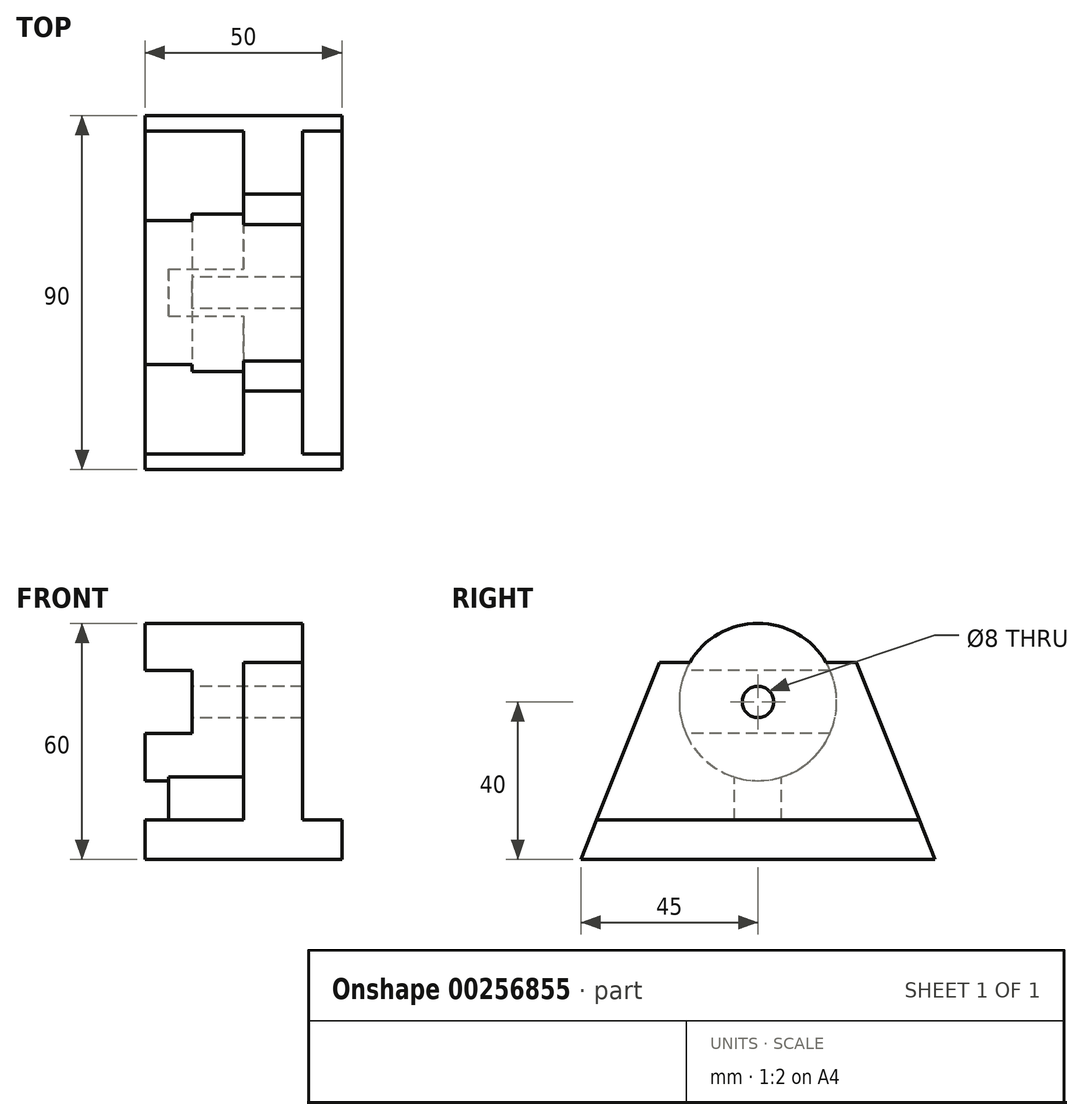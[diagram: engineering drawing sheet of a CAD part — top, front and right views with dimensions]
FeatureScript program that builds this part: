
annotation { "Feature Type Name" : "Feature", "Feature Type Description" : "" }
export const myFeature = defineFeature(function(context is Context, id is Id, definition is map)
    precondition{}
    {
        {
            var Q0;
            Q0=qCreatedBy(makeId("Right.planeOp"),FACE);
            var sketch = newSketch(context, id + "F0", { "sketchPlane" : qUnion([Q0])});
            skLineSegment(sketch, "E0.bottom", {"start": v(-45, 25) * mm, "end": v(45, 25) * mm});
            skLineSegment(sketch, "E0.top", {"start": v(-45, -25) * mm, "end": v(45, -25) * mm});
            skLineSegment(sketch, "E0.left", {"start": v(-45, 25) * mm, "end": v(-45, -25) * mm});
            skLineSegment(sketch, "E0.right", {"start": v(45, 25) * mm, "end": v(45, -25) * mm});
            skPoint(sketch, "E0.middle", {"position": v(0, 0) * mm});
            skLineSegment(sketch, "E1", {"start": v(-25, 25) * mm, "end": v(-25, -25) * mm});
            skLineSegment(sketch, "E2", {"start": v(25, 25) * mm, "end": v(25, -25) * mm});
            skLineSegment(sketch, "E3", {"start": v(45, -15) * mm, "end": v(-45, -15) * mm});
            skLineSegment(sketch, "E4", {"start": v(25, 25) * mm, "end": v(45, -25) * mm});
            skLineSegment(sketch, "E5", {"start": v(-45, -25) * mm, "end": v(-25, 25) * mm});
            skLineSegment(sketch, "E6", {"start": v(-25, 15) * mm, "end": v(25, 15) * mm});
            skCircle(sketch, "E7", {"center": v(0, 15) * mm, "radius": 20 * mm});
            skSolve(sketch);
        }
        {
            var Q0;
            {var subQ1=sQuery(id+"F0.wireOp",EDGE,"E0.top");var subQ3=sQuery(id+"F0.wireOp",EDGE,"E2");var subQ4=makeQuery(id+"F0.imprint","INTERSECT",VERTEX,{"derivedFrom":[subQ1,subQ3]});Q0=makeQuery(id+"F0.imprint","IMPRINT",FACE,{"disambiguationData":[TD([[makeQuery(id+"F0.imprint","IMPRINT",EDGE,{"disambiguationData":[TD([[subQ4,1.0]])],"derivedFrom":subQ3}),1.0]])]});}
            var Q1;
            {var subQ0=sQuery(id+"F0.wireOp",EDGE,"E1");var subQ1=sQuery(id+"F0.wireOp",EDGE,"E0.top");var subQ2=makeQuery(id+"F0.imprint","INTERSECT",VERTEX,{"derivedFrom":[subQ1,subQ0]});Q1=makeQuery(id+"F0.imprint","IMPRINT",FACE,{"disambiguationData":[TD([[makeQuery(id+"F0.imprint","IMPRINT",EDGE,{"disambiguationData":[TD([[subQ2,-1.0]])],"derivedFrom":subQ1}),1.0]])]});}
            var Q2;
            {var subQ1=sQuery(id+"F0.wireOp",EDGE,"E0.top");var subQ3=sQuery(id+"F0.wireOp",EDGE,"E1");var subQ4=makeQuery(id+"F0.imprint","INTERSECT",VERTEX,{"derivedFrom":[subQ1,subQ3]});Q2=makeQuery(id+"F0.imprint","IMPRINT",FACE,{"disambiguationData":[TD([[makeQuery(id+"F0.imprint","IMPRINT",EDGE,{"disambiguationData":[TD([[subQ4,1.0]])],"derivedFrom":subQ3}),-1.0]])]});}
            extrude(context, id + "F1", {"entities" : qUnion([Q0, Q1, Q2]), "endBound" : BoundingType.SYMMETRIC, "depth" : 50 * mm});
        }
        {
            var Q0;
            {var subQ0=sQuery(id+"F0.wireOp",EDGE,"E1");var subQ5=sQuery(id+"F0.wireOp",EDGE,"E3");var subQ6=makeQuery(id+"F0.imprint","INTERSECT",VERTEX,{"derivedFrom":[subQ0,subQ5]});Q0=makeQuery(id+"F0.imprint","IMPRINT",FACE,{"disambiguationData":[TD([[makeQuery(id+"F0.imprint","IMPRINT",EDGE,{"disambiguationData":[TD([[subQ6,1.0]])],"derivedFrom":subQ5}),-1.0]])]});}
            var Q1;
            {var subQ1=sQuery(id+"F0.wireOp",EDGE,"E2");var subQ3=sQuery(id+"F0.wireOp",EDGE,"E3");var subQ4=makeQuery(id+"F0.imprint","INTERSECT",VERTEX,{"derivedFrom":[subQ1,subQ3]});Q1=makeQuery(id+"F0.imprint","IMPRINT",FACE,{"disambiguationData":[TD([[makeQuery(id+"F0.imprint","IMPRINT",EDGE,{"disambiguationData":[TD([[subQ4,1.0]])],"derivedFrom":subQ3}),-1.0]])]});}
            var Q2;
            {var subQ1=sQuery(id+"F0.wireOp",EDGE,"E1");var subQ3=sQuery(id+"F0.wireOp",EDGE,"E3");var subQ4=makeQuery(id+"F0.imprint","INTERSECT",VERTEX,{"derivedFrom":[subQ1,subQ3]});Q2=makeQuery(id+"F0.imprint","IMPRINT",FACE,{"disambiguationData":[TD([[makeQuery(id+"F0.imprint","IMPRINT",EDGE,{"disambiguationData":[TD([[subQ4,-1.0]])],"derivedFrom":subQ3}),-1.0]])]});}
            var Q3;
            {var subQ0=sQuery(id+"F0.wireOp",EDGE,"E1");var subQ5=sQuery(id+"F0.wireOp",EDGE,"E6");var subQ7=makeQuery(id+"F0.imprint","INTERSECT",VERTEX,{"derivedFrom":[subQ0,subQ5]});Q3=makeQuery(id+"F0.imprint","IMPRINT",FACE,{"disambiguationData":[TD([[makeQuery(id+"F0.imprint","IMPRINT",EDGE,{"disambiguationData":[TD([[subQ7,-1.0]])],"derivedFrom":subQ5}),1.0]])]});}
            var Q4;
            {var subQ0=sQuery(id+"F0.wireOp",EDGE,"E2");var subQ5=sQuery(id+"F0.wireOp",EDGE,"E6");var subQ6=makeQuery(id+"F0.imprint","INTERSECT",VERTEX,{"derivedFrom":[subQ0,subQ5]});Q4=makeQuery(id+"F0.imprint","IMPRINT",FACE,{"disambiguationData":[TD([[makeQuery(id+"F0.imprint","IMPRINT",EDGE,{"disambiguationData":[TD([[subQ6,1.0]])],"derivedFrom":subQ5}),1.0]])]});}
            extrude(context, id + "F2", {"entities" : qUnion([Q0, Q1, Q2, Q3, Q4]), "operationType" : NewBodyOperationType.ADD, "depth" : 15 * mm});
        }
        {
            var Q0;
            {var subQ0=sQuery(id+"F0.wireOp",EDGE,"E7");var subQ1=sQuery(id+"F0.wireOp",EDGE,"E0.bottom");var subQ2=makeQuery(id+"F0.imprint","INTERSECT",VERTEX,{"disambiguationData":[OD(0.0)],"derivedFrom":[subQ1,subQ0]});Q0=makeQuery(id+"F0.imprint","IMPRINT",FACE,{"disambiguationData":[TD([[makeQuery(id+"F0.imprint","IMPRINT",EDGE,{"disambiguationData":[TD([[subQ2,-1.0]])],"derivedFrom":subQ1}),1.0]])]});}
            var Q1;
            {var subQ0=sQuery(id+"F0.wireOp",EDGE,"E7");var subQ1=sQuery(id+"F0.wireOp",EDGE,"E0.bottom");var subQ2=makeQuery(id+"F0.imprint","INTERSECT",VERTEX,{"disambiguationData":[OD(0.0)],"derivedFrom":[subQ1,subQ0]});Q1=makeQuery(id+"F0.imprint","IMPRINT",FACE,{"disambiguationData":[TD([[makeQuery(id+"F0.imprint","IMPRINT",EDGE,{"disambiguationData":[TD([[subQ2,-1.0]])],"derivedFrom":subQ1}),-1.0]])]});}
            var Q2;
            {var subQ0=sQuery(id+"F0.wireOp",EDGE,"E7");var subQ1=sQuery(id+"F0.wireOp",EDGE,"E6");var subQ2=makeQuery(id+"F0.imprint","INTERSECT",VERTEX,{"disambiguationData":[OD(0.0)],"derivedFrom":[subQ1,subQ0]});Q2=makeQuery(id+"F0.imprint","IMPRINT",FACE,{"disambiguationData":[TD([[makeQuery(id+"F0.imprint","IMPRINT",EDGE,{"disambiguationData":[TD([[subQ2,-1.0]])],"derivedFrom":subQ1}),-1.0]])]});}
            extrude(context, id + "F3", {"entities" : qUnion([Q0, Q1, Q2]), "operationType" : NewBodyOperationType.ADD, "depth" : 15 * mm, "hasSecondDirection" : true, "secondDirectionOppositeDirection" : true, "secondDirectionDepth" : 25 * mm});
        }
        {
            var Q0;
            Q0=makeQuery(id+"F3.opExtrude","CAP_FACE",FACE,{"disambiguationData":[OSD([sQuery(id+"F0.wireOp",EDGE,"E7")])],"isStart":true});
            var sketch = newSketch(context, id + "F4", { "sketchPlane" : qUnion([Q0])});
            skPoint(sketch, "E8", {"position": v(0, 15) * mm});
            skLineSegment(sketch, "E9.bottom", {"start": v(20, 35) * mm, "end": v(-20, 35) * mm});
            skLineSegment(sketch, "E9.top", {"start": v(20, -5) * mm, "end": v(-20, -5) * mm});
            skLineSegment(sketch, "E9.left", {"start": v(20, 35) * mm, "end": v(20, -5) * mm});
            skLineSegment(sketch, "E9.right", {"start": v(-20, 35) * mm, "end": v(-20, -5) * mm});
            skLineSegment(sketch, "E10", {"start": v(-20, 15) * mm, "end": v(20, 15) * mm});
            skLineSegment(sketch, "E11", {"start": v(-20, 23) * mm, "end": v(20, 23) * mm});
            skLineSegment(sketch, "E12", {"start": v(-20, 7) * mm, "end": v(20, 7) * mm});
            skSolve(sketch);
        }
        {
            var Q0;
            {var subQ0=sQuery(id+"F4.wireOp",EDGE,"E10");Q0=makeQuery(id+"F4.imprint","IMPRINT",FACE,{"disambiguationData":[TD([[makeQuery(id+"F4.imprint","IMPRINT",EDGE,{"derivedFrom":subQ0}),1.0]])]});}
            var Q1;
            {var subQ0=sQuery(id+"F4.wireOp",EDGE,"E10");Q1=makeQuery(id+"F4.imprint","IMPRINT",FACE,{"disambiguationData":[TD([[makeQuery(id+"F4.imprint","IMPRINT",EDGE,{"derivedFrom":subQ0}),-1.0]])]});}
            extrude(context, id + "F5", {"entities" : qUnion([Q0, Q1]), "operationType" : NewBodyOperationType.REMOVE, "oppositeDirection" : true, "depth" : 12 * mm});
        }
        {
            var Q0;
            Q0=sQuery(id+"F4.wireOp",VERTEX,"E8");
            var Q1;
            Q1=makeQuery(id+"F1.opExtrude","SWEPT_BODY",BODY,{"disambiguationData":[OSD([sQuery(id+"F0.wireOp",EDGE,"E0.top"),sQuery(id+"F0.wireOp",EDGE,"E3"),sQuery(id+"F0.wireOp",EDGE,"E4"),sQuery(id+"F0.wireOp",EDGE,"E5")])]});
            hole(context, id + "F6", {"style" : HoleStyle.SIMPLE, "endStyle" : HoleEndStyle.THROUGH, "holeDiameter" : 8 * mm, "tappedDepth" : 12 * mm, "tapClearance" : 3, "locations" : qUnion([Q0]), "scope" : qUnion([Q1])});
        }
        {
            var Q0;
            Q0=qCreatedBy(makeId("Top.planeOp"),FACE);
            var sketch = newSketch(context, id + "F7", { "sketchPlane" : qUnion([Q0])});
            skLineSegment(sketch, "E13.bottom", {"start": v(25, -45) * mm, "end": v(-25, -45) * mm});
            skLineSegment(sketch, "E13.top", {"start": v(25, 45) * mm, "end": v(-25, 45) * mm});
            skLineSegment(sketch, "E13.left", {"start": v(25, -45) * mm, "end": v(25, 45) * mm});
            skLineSegment(sketch, "E13.right", {"start": v(-25, -45) * mm, "end": v(-25, 45) * mm});
            skPoint(sketch, "E13.middle", {"position": v(0, 0) * mm});
            skLineSegment(sketch, "E14", {"start": v(-19, 45) * mm, "end": v(-19, -45) * mm});
            skLineSegment(sketch, "E15", {"start": v(0, 45) * mm, "end": v(0, -45) * mm});
            skLineSegment(sketch, "E16", {"start": v(25, 6) * mm, "end": v(-25, 6) * mm});
            skLineSegment(sketch, "E17", {"start": v(25, -6) * mm, "end": v(-25, -6) * mm});
            skSolve(sketch);
        }
        {
            var Q0;
            {var subQ0=sQuery(id+"F7.wireOp",EDGE,"E16");var subQ1=sQuery(id+"F7.wireOp",EDGE,"E14");var subQ2=makeQuery(id+"F7.imprint","INTERSECT",VERTEX,{"derivedFrom":[subQ1,subQ0]});Q0=makeQuery(id+"F7.imprint","IMPRINT",FACE,{"disambiguationData":[TD([[makeQuery(id+"F7.imprint","IMPRINT",EDGE,{"disambiguationData":[TD([[subQ2,-1.0]])],"derivedFrom":subQ1}),1.0]])]});}
            extrude(context, id + "F8", {"entities" : qUnion([Q0]), "operationType" : NewBodyOperationType.ADD, "oppositeDirection" : true, "depth" : 25 * mm});
        }
    });
